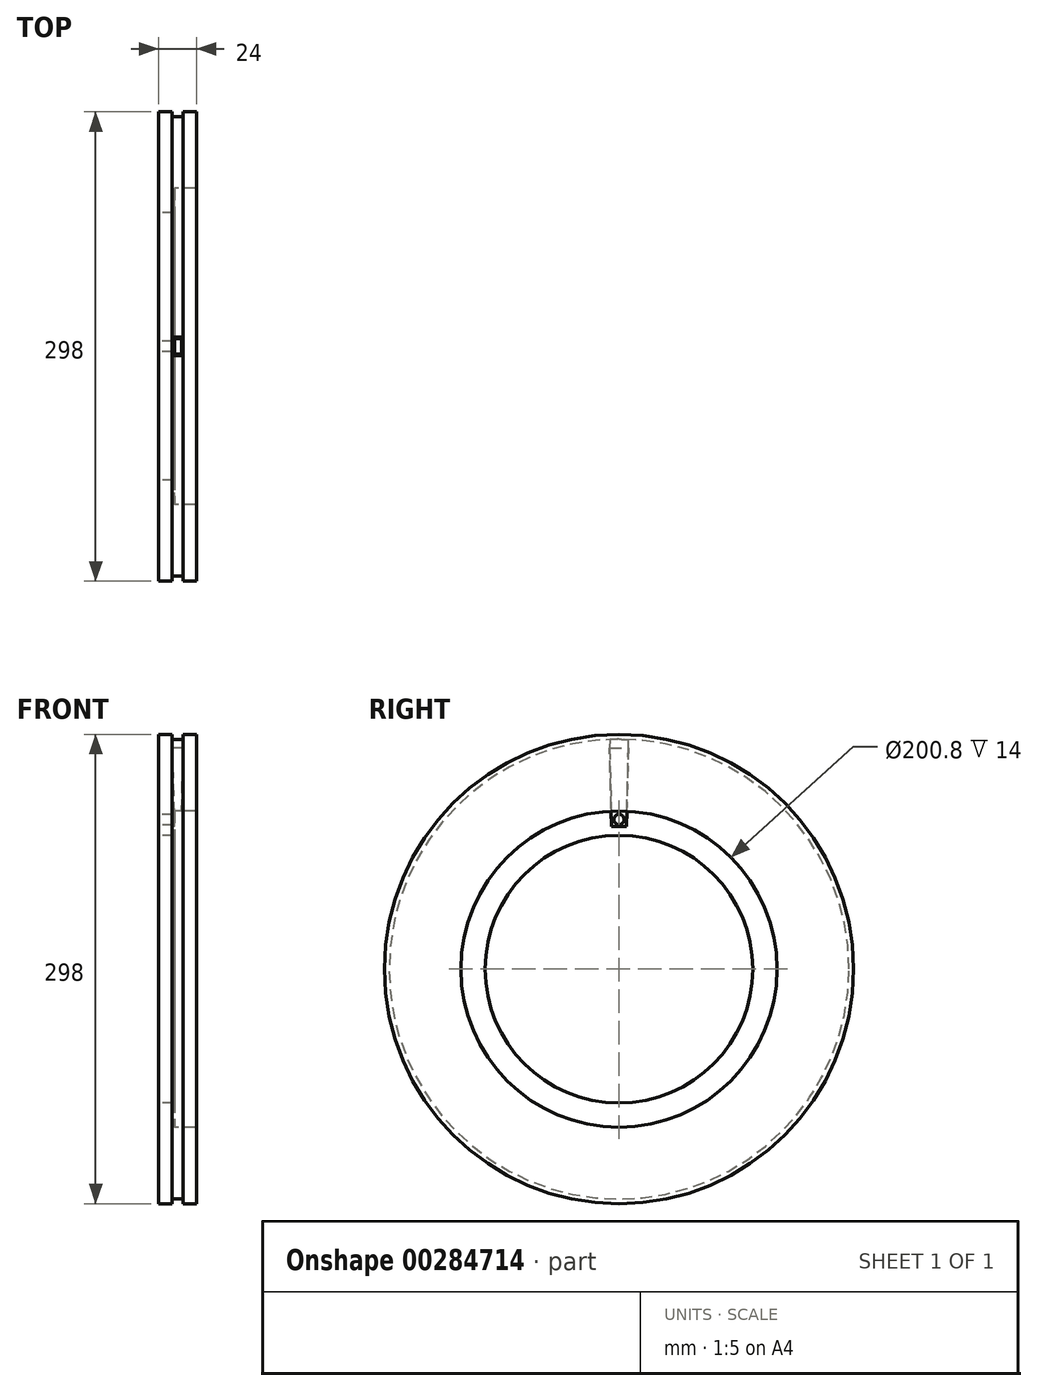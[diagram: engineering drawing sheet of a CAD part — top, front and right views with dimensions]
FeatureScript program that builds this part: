
annotation { "Feature Type Name" : "Feature", "Feature Type Description" : "" }
export const myFeature = defineFeature(function(context is Context, id is Id, definition is map)
    precondition{}
    {
        {
            var Q0;
            Q0=qCreatedBy(makeId("Front.planeOp"),FACE);
            var sketch = newSketch(context, id + "F0", { "sketchPlane" : qUnion([Q0])});
            skLineSegment(sketch, "E0", {"start": v(0, 0) * mm, "end": v(0, 149) * mm});
            skLineSegment(sketch, "E1", {"start": v(-17, 149) * mm, "end": v(-24, 149) * mm});
            skLineSegment(sketch, "E2", {"start": v(-24, 149) * mm, "end": v(-24, 85) * mm});
            skLineSegment(sketch, "E3", {"start": v(-24, 85) * mm, "end": v(-14, 85) * mm});
            skLineSegment(sketch, "E4", {"start": v(-14, 85) * mm, "end": v(-14, 100.4) * mm});
            skLineSegment(sketch, "E5", {"start": v(-39.7, 0) * mm, "end": v(35.3, 0) * mm, "construction": true});
            skLineSegment(sketch, "E6", {"start": v(0, 149) * mm, "end": v(-8.5, 149) * mm});
            skLineSegment(sketch, "E7", {"start": v(-14, 100.4) * mm, "end": v(0, 100.4) * mm});
            skLineSegment(sketch, "E8.bottom", {"start": v(-8.5, 146) * mm, "end": v(-15.5, 146) * mm});
            skLineSegment(sketch, "E8.left", {"start": v(-8.5, 146) * mm, "end": v(-8.5, 149) * mm});
            skLineSegment(sketch, "E8.right", {"start": v(-15.5, 146) * mm, "end": v(-15.5, 149) * mm});
            skLineSegment(sketch, "E9.trimOffspring", {"start": v(-15.5, 149) * mm, "end": v(-17, 149) * mm});
            skSolve(sketch);
        }
        {
            var Q0;
            {var subQ0=sQuery(id+"F0.wireOp",EDGE,"E1");Q0=makeQuery(id+"F0.imprint","IMPRINT",FACE,{"disambiguationData":[TD([[makeQuery(id+"F0.imprint","IMPRINT",EDGE,{"derivedFrom":subQ0}),1.0]])]});}
            var Q1;
            Q1=makeQuery(id+"F0.imprint","IMPRINT",FACE,{"disambiguationData":[TD([[makeQuery(id+"F0.imprint","IMPRINT",EDGE,{"derivedFrom":sQuery(id+"F0.wireOp",EDGE,"7fXnF028-M3xj-EacU-AWOU-BzuDLJln6x9B")}),-1.0]])]});
            var Q2;
            {var subQ1=sQuery(id+"F0.wireOp",EDGE,"in6MgAQn-sbUD-tzpW-YmQU-YWNDP7CuIbv5");Q2=makeQuery(id+"F0.imprint","IMPRINT",FACE,{"disambiguationData":[TD([[makeQuery(id+"F0.imprint","IMPRINT",EDGE,{"derivedFrom":subQ1}),1.0]])]});}
            var Q3;
            Q3=sQuery(id+"F0.wireOp",EDGE,"E5");
            var Q4;
            Q4=sQuery(id+"F0.wireOp",EDGE,"E0");
            var Q5;
            Q5=sQuery(id+"F0.wireOp",EDGE,"in6MgAQn-sbUD-tzpW-YmQU-YWNDP7CuIbv5");
            var Q6;
            Q6=sQuery(id+"F0.wireOp",EDGE,"7fXnF028-M3xj-EacU-AWOU-BzuDLJln6x9B");
            var Q7;
            Q7=sQuery(id+"F0.wireOp",EDGE,"CdqGMiTu-W7TX-hF68-SEuM-eFApA8aCY1ZB");
            var Q8;
            Q8=sQuery(id+"F0.wireOp",EDGE,"Adw1gT33-leLd-TGds-6zjy-wcVkvDirY0WB");
            var Q9;
            Q9=sQuery(id+"F0.wireOp",EDGE,"mUVdKNK3-K0ie-Oo0J-aP3B-C1tAP6vjT7Tc");
            var Q10;
            Q10=sQuery(id+"F0.wireOp",EDGE,"Rnxdy38E-YgJg-5Qse-s6hE-6pi8oPfkeCxi");
            var Q11;
            Q11=sQuery(id+"F0.wireOp",EDGE,"E1");
            var Q12;
            Q12=sQuery(id+"F0.wireOp",EDGE,"E2");
            var Q13;
            Q13=sQuery(id+"F0.wireOp",EDGE,"E4");
            var Q14;
            Q14=sQuery(id+"F0.wireOp",EDGE,"E3");
            var Q15;
            Q15=sQuery(id+"F0.wireOp",EDGE,"E5");
            revolve(context, id + "F1", {"entities" : qUnion([Q0, Q1, Q2]), "surfaceEntities" : qUnion([Q3, Q4, Q5, Q6, Q7, Q8, Q9, Q10, Q11, Q12, Q13, Q14]), "axis" : qUnion([Q15]), "revolveType" : RevolveType.FULL});
        }
        {
            var Q0;
            Q0=qCreatedBy(makeId("Top.planeOp"),FACE);
            cPlane(context, id + "F2", {"entities" : qUnion([Q0]), "cplaneType" : CPlaneType.OFFSET, "offset" : 140.5 * mm, "width" : 150 * mm, "height" : 150 * mm});
        }
        {
            var Q0;
            Q0=qCreatedBy(id+"F2.planeOp",FACE);
            var sketch = newSketch(context, id + "F3", { "sketchPlane" : qUnion([Q0])});
            skLineSegment(sketch, "E10", {"start": v(0, 0) * mm, "end": v(-12, 0) * mm, "construction": true});
            skLineSegment(sketch, "E11.bottom", {"start": v(-8.5, -6) * mm, "end": v(-15.5, -6) * mm});
            skLineSegment(sketch, "E11.top", {"start": v(-8.5, 6) * mm, "end": v(-15.5, 6) * mm});
            skLineSegment(sketch, "E11.left", {"start": v(-8.5, -6) * mm, "end": v(-8.5, 6) * mm});
            skLineSegment(sketch, "E11.right", {"start": v(-15.5, -6) * mm, "end": v(-15.5, 6) * mm});
            skPoint(sketch, "E11.middle", {"position": v(-12, 0) * mm});
            skSolve(sketch);
        }
        {
            var Q0;
            Q0=qSketchRegion(id+"F3",true);
            extrude(context, id + "F4", {"entities" : qUnion([Q0]), "operationType" : NewBodyOperationType.REMOVE, "endBound" : BoundingType.SYMMETRIC, "oppositeDirection" : true, "offsetDistance" : 25 * mm, "depth" : 100 * mm, "hasDraft" : true, "draftAngle" : 1.5 * degree, "draftPullDirection" : true});
        }
        {
            var Q0;
            Q0=qCreatedBy(makeId("Right.planeOp"),FACE);
            cPlane(context, id + "F5", {"entities" : qUnion([Q0]), "cplaneType" : CPlaneType.OFFSET, "offset" : 24 * mm, "oppositeDirection" : true, "width" : 150 * mm, "height" : 150 * mm});
        }
        {
            var Q0;
            Q0=qCreatedBy(id+"F5.planeOp",FACE);
            var sketch = newSketch(context, id + "F6", { "sketchPlane" : qUnion([Q0])});
            skCircle(sketch, "E12.0", {"center": v(0, 0) * mm, "radius": 85 * mm});
            skPoint(sketch, "E13", {"position": v(0, 95) * mm});
            skCircle(sketch, "E14", {"center": v(0, 95) * mm, "radius": 3.3 * mm});
            skSolve(sketch);
        }
        {
            var Q0;
            Q0=makeQuery(id+"F6.imprint","IMPRINT",FACE,{"disambiguationData":[TD([[makeQuery(id+"F6.imprint","IMPRINT",EDGE,{"derivedFrom":sQuery(id+"F6.wireOp",EDGE,"E14")}),1.0]])]});
            extrude(context, id + "F7", {"entities" : qUnion([Q0]), "operationType" : NewBodyOperationType.REMOVE, "offsetDistance" : 25 * mm, "depth" : 46 * mm});
        }
    });
